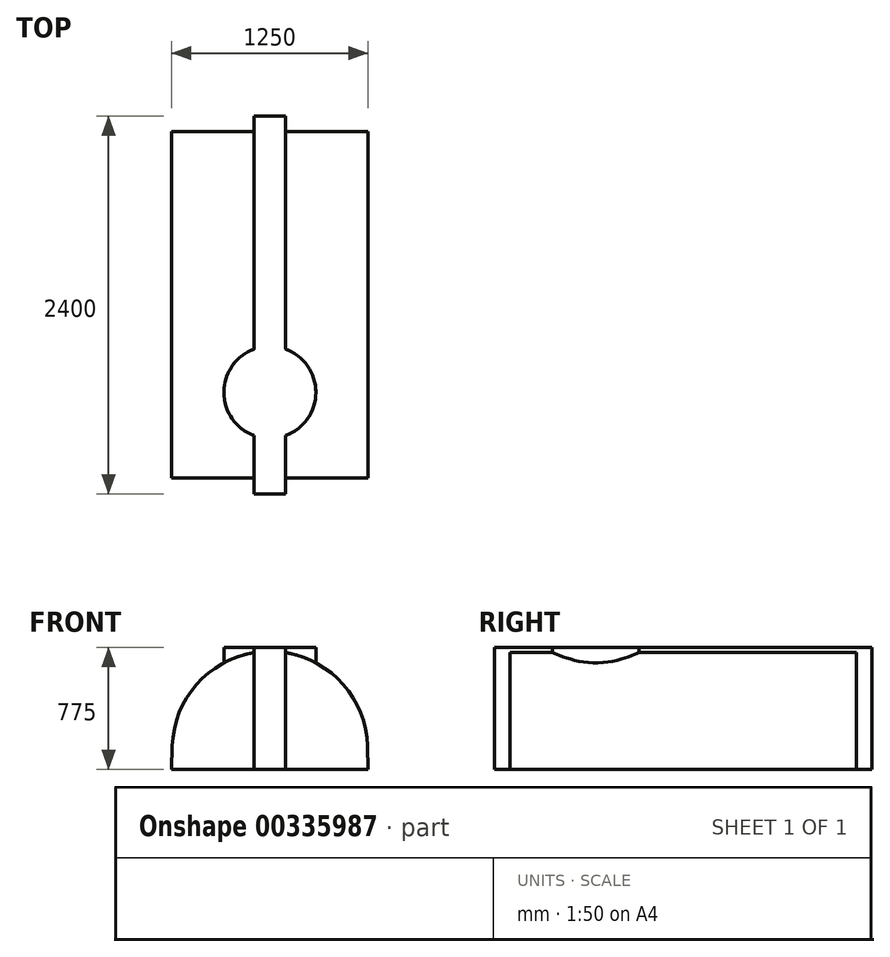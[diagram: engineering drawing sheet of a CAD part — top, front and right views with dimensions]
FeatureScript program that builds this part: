
annotation { "Feature Type Name" : "Feature", "Feature Type Description" : "" }
export const myFeature = defineFeature(function(context is Context, id is Id, definition is map)
    precondition{}
    {
        {
            var Q0;
            Q0=qCreatedBy(makeId("Front.planeOp"),FACE);
            var sketch = newSketch(context, id + "F0", { "sketchPlane" : qUnion([Q0])});
            skLineSegment(sketch, "E0", {"start": v(-620.06, 150) * mm, "end": v(-625, 0) * mm});
            skLineSegment(sketch, "E1", {"start": v(-625, 0) * mm, "end": v(0, 0) * mm});
            skLineSegment(sketch, "E2", {"start": v(-620.06, 150) * mm, "end": v(-110.23, 150) * mm, "construction": true});
            skLineSegment(sketch, "E3", {"start": v(-707.65, 750) * mm, "end": v(0, 750) * mm, "construction": true});
            skLineSegment(sketch, "E4", {"start": v(0, 0) * mm, "end": v(0, 843.39) * mm, "construction": true});
            skArc(sketch, "E5", {"start": v(-620.06, 150) * mm, "mid": v(-431.42, 575.44) * mm, "end": v(0, 750) * mm});
            skLineSegment(sketch, "E6.MirrorCS", {"start": v(620.06, 150) * mm, "end": v(625, 0) * mm});
            skLineSegment(sketch, "E7.MirrorCS", {"start": v(625, 0) * mm, "end": v(0, 0) * mm});
            skArc(sketch, "E8.MirrorCS", {"start": v(620.06, 150) * mm, "mid": v(431.42, 575.44) * mm, "end": v(0, 750) * mm});
            skSolve(sketch);
        }
        {
            var Q0;
            Q0=qSketchRegion(id+"F0",true);
            extrude(context, id + "F1", {"entities" : qUnion([Q0]), "endBound" : BoundingType.SYMMETRIC, "depth" : 2200 * mm});
        }
        {
            var Q0;
            Q0=qCreatedBy(makeId("Top.planeOp"),FACE);
            var sketch = newSketch(context, id + "F2", { "sketchPlane" : qUnion([Q0])});
            skLineSegment(sketch, "E9.bottom", {"start": v(100, 1200) * mm, "end": v(-100, 1200) * mm});
            skLineSegment(sketch, "E9.top", {"start": v(100, -1200) * mm, "end": v(-100, -1200) * mm});
            skLineSegment(sketch, "E9.left", {"start": v(100, 1200) * mm, "end": v(100, -1200) * mm});
            skLineSegment(sketch, "E9.right", {"start": v(-100, 1200) * mm, "end": v(-100, -1200) * mm});
            skPoint(sketch, "E9.middle", {"position": v(0, 0) * mm});
            skCircle(sketch, "E10", {"center": v(0, -555.08) * mm, "radius": 292.04 * mm});
            skSolve(sketch);
        }
        {
            var Q0;
            Q0 = qSketchRegion(id + "F2", true);
            extrude(context, id + "F3", {"entities" : qUnion([Q0]), "operationType" : NewBodyOperationType.ADD, "depth" : 775 * mm});
        }
    });
